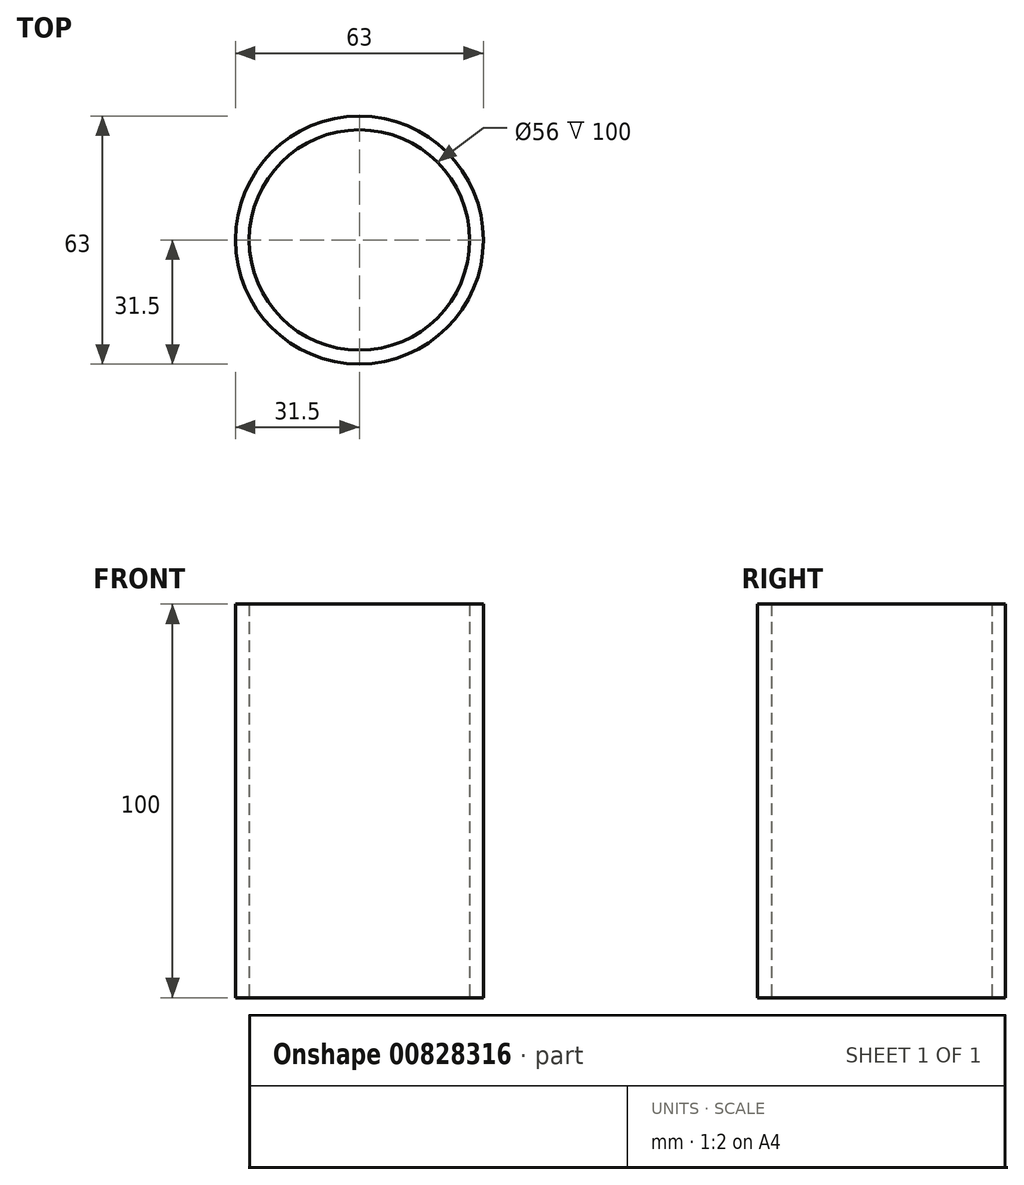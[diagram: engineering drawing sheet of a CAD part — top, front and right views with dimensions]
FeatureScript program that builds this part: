
annotation { "Feature Type Name" : "Feature", "Feature Type Description" : "" }
export const myFeature = defineFeature(function(context is Context, id is Id, definition is map)
    precondition{}
    {
        {
            var Q0;
            Q0=qCreatedBy(makeId("Top.planeOp"),FACE);
            var sketch = newSketch(context, id + "F0", { "sketchPlane" : qUnion([Q0])});
            skCircle(sketch, "E0", {"center": v(0, 0) * mm, "radius": 31.5 * mm});
            skCircle(sketch, "E1", {"center": v(0, 0) * mm, "radius": 28 * mm});
            skSolve(sketch);
        }
        {
            var Q0;
            Q0=makeQuery(id+"F0.imprint","IMPRINT",FACE,{"disambiguationData":[TD([[makeQuery(id+"F0.imprint","IMPRINT",EDGE,{"derivedFrom":sQuery(id+"F0.wireOp",EDGE,"E0")}),1.0]])]});
            extrude(context, id + "F1", {"entities" : qUnion([Q0]), "depth" : 100 * mm, "offsetDistance" : 25 * mm});
        }
    });
